FCSTD DOCUMENT  (FreeCAD 0.17R13541 (Git))
Label: Xtrusion4mm
License: All rights reserved
LicenseURL: http://en.wikipedia.org/wiki/All_rights_reserved
objects: Sketcher::SketchObject×1
note: 1 computed .brp shape members not serialized (recipe doc carries the construction recipe); baked Part::Feature solids carry a one-line shape summary decoded from their .brp

FEATURE [Sketcher::SketchObject] Sketch
  sketch-geometry (24):
    g0: LineSegment StartX=-73.9851 StartY=-24.6214 StartZ=0 EndX=-61.5896 EndY=-24.6214 EndZ=0
    g1: LineSegment StartX=-61.5896 StartY=-24.6214 StartZ=0 EndX=-65.7593 EndY=-20.4517 EndZ=0
    g2: LineSegment StartX=-65.7593 StartY=-20.4517 StartZ=0 EndX=-53.4199 EndY=-20.4517 EndZ=0
    g3: LineSegment StartX=-53.4199 StartY=-20.4517 StartZ=0 EndX=-57.5896 EndY=-24.6214 EndZ=0
    g4: LineSegment StartX=-57.5896 StartY=-24.6214 StartZ=0 EndX=-45.1941 EndY=-24.6214 EndZ=0
    g5: LineSegment StartX=-45.1941 StartY=-24.6214 StartZ=0 EndX=-45.1941 EndY=-12.2258 EndZ=0
    g6: LineSegment StartX=-45.1941 StartY=-12.2258 StartZ=0 EndX=-49.3638 EndY=-16.3955 EndZ=0
    g7: LineSegment StartX=-49.3638 StartY=-16.3955 StartZ=0 EndX=-49.3638 EndY=-4.05614 EndZ=0
    g8: LineSegment StartX=-49.3638 StartY=-4.05614 StartZ=0 EndX=-45.1941 EndY=-8.22584 EndZ=0
    g9: LineSegment StartX=-45.1941 StartY=-8.22584 StartZ=0 EndX=-45.1941 EndY=4.1697 EndZ=0
    g10: LineSegment StartX=-45.1941 StartY=4.1697 StartZ=0 EndX=-57.5896 EndY=4.1697 EndZ=0
    g11: LineSegment StartX=-57.5896 StartY=4.1697 StartZ=0 EndX=-53.4199 EndY=0 EndZ=0
    g12: LineSegment StartX=-53.4199 StartY=0 StartZ=0 EndX=-65.7593 EndY=0 EndZ=0
    g13: LineSegment StartX=-65.7593 StartY=0 StartZ=0 EndX=-61.5896 EndY=4.1697 EndZ=0
    g14: LineSegment StartX=-61.5896 StartY=4.1697 StartZ=0 EndX=-73.9851 EndY=4.1697 EndZ=0
    g15: LineSegment StartX=-73.9851 StartY=4.1697 StartZ=0 EndX=-73.9851 EndY=-8.22584 EndZ=0
    g16: LineSegment StartX=-73.9851 StartY=-8.22584 StartZ=0 EndX=-69.8154 EndY=-4.05614 EndZ=0
    g17: LineSegment StartX=-69.8154 StartY=-4.05614 StartZ=0 EndX=-69.8154 EndY=-16.3955 EndZ=0
    g18: LineSegment StartX=-69.8154 StartY=-16.3955 StartZ=0 EndX=-73.9851 EndY=-12.2258 EndZ=0
    g19: LineSegment StartX=-73.9851 StartY=-12.2258 StartZ=0 EndX=-73.9851 EndY=-24.6214 EndZ=0
    g20: LineSegment [constr] StartX=-61.5896 StartY=-24.6214 StartZ=0 EndX=-57.5896 EndY=-24.6214 EndZ=0
    g21: LineSegment [constr] StartX=-61.5896 StartY=4.1697 StartZ=0 EndX=-57.5896 EndY=4.1697 EndZ=0
    g22: LineSegment [constr] StartX=-45.1941 StartY=-8.22584 StartZ=0 EndX=-45.1941 EndY=-12.2258 EndZ=0
    g23: LineSegment [constr] StartX=-73.9851 StartY=-8.22584 StartZ=0 EndX=-73.9851 EndY=-12.2258 EndZ=0
  constraints (69):
    c: Horizontal(g0)
    c: Coincident(g0,g1)
    c: Coincident(g1,g2)
    c: Horizontal(g2)
    c: Coincident(g2,g3)
    c: Coincident(g3,g4)
    c: Horizontal(g4)
    c: Coincident(g4,g5)
    c: Vertical(g5)
    c: Coincident(g5,g6)
    c: Coincident(g6,g7)
    c: Vertical(g7)
    c: Coincident(g7,g8)
    c: Coincident(g8,g9)
    c: Vertical(g9)
    c: Coincident(g9,g10)
    c: Horizontal(g10)
    c: Coincident(g10,g11)
    c: Coincident(g11,g12)
    c: PointOnObject(g12,g-1)
    c: Horizontal(g12)
    c: Coincident(g12,g13)
    c: Coincident(g13,g14)
    c: Horizontal(g14)
    c: Coincident(g14,g15)
    c: Vertical(g15)
    c: Coincident(g15,g16)
    c: Coincident(g16,g17)
    c: Vertical(g17)
    c: Coincident(g17,g18)
    c: Coincident(g18,g19)
    c: Vertical(g19)
    c: Equal(g14,g10)
    c: Equal(g10,g9)
    c: Equal(g9,g5)
    c: Equal(g5,g4)
    c: Equal(g4,g0)
    c: Equal(g0,g19)
    c: Equal(g19,g15)
    c: Equal(g17,g12)
    c: Equal(g12,g7)
    c: Equal(g7,g2)
    c: Angle(g1,g0) = 0.785398
    c: Angle(g19,g18) = 0.785398
    c: Angle(g4,g3) = 0.785398
    c: Angle(g6,g5) = 0.785398
    c: Angle(g9,g8) = 0.785398
    c: Angle(g11,g10) = 0.785398
    c: Angle(g14,g13) = 0.785398
    c: Angle(g16,g15) = 0.785398
    c: Equal(g16,g13)
    c: Equal(g13,g11)
    c: Equal(g11,g8)
    c: Equal(g8,g6)
    c: Equal(g6,g3)
    c: Equal(g3,g1)
    c: Equal(g1,g18)
    c: Coincident(g20,g0)
    c: Coincident(g20,g3)
    c: Coincident(g21,g13)
    c: Coincident(g21,g10)
    c: Coincident(g22,g8)
    c: Coincident(g22,g5)
    c: Coincident(g23,g15)
    c: Coincident(g23,g18)
    c: Equal(g23,g21)
    c: Equal(g21,g22)
    c: Equal(g22,g20)
    c: Distance(g21) = 4
